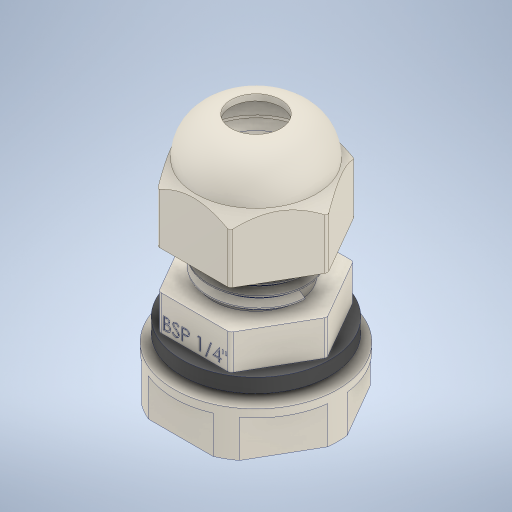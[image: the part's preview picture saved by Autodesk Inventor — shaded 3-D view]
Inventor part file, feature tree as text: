
AUTODESK INVENTOR PART (.ipt)
format: ipt  version: 2024 (Build 280153000, 153)  size: 819,712 bytes
history: native  units: in
note: dims shown in document units (in); Inventor stores cm internally (conversion verified against a paired STEP export)
features: sketch x2, other x2
ambient origin geometry x8: Origin, YZ Plane, XZ Plane, XY Plane, X Axis, Y Axis, Z Axis, Center Point
bodies: Solid1 (feature_tree), Solid2 (feature_tree)
feature tree (4):
  sketch  "Sketch1"
  sketch  "Sketch2"
  other  "Prensa Cabo 1.4 BSP-1-solid1"
  other  "Prensa Cabo 1.4 BSP-1-solid2"
